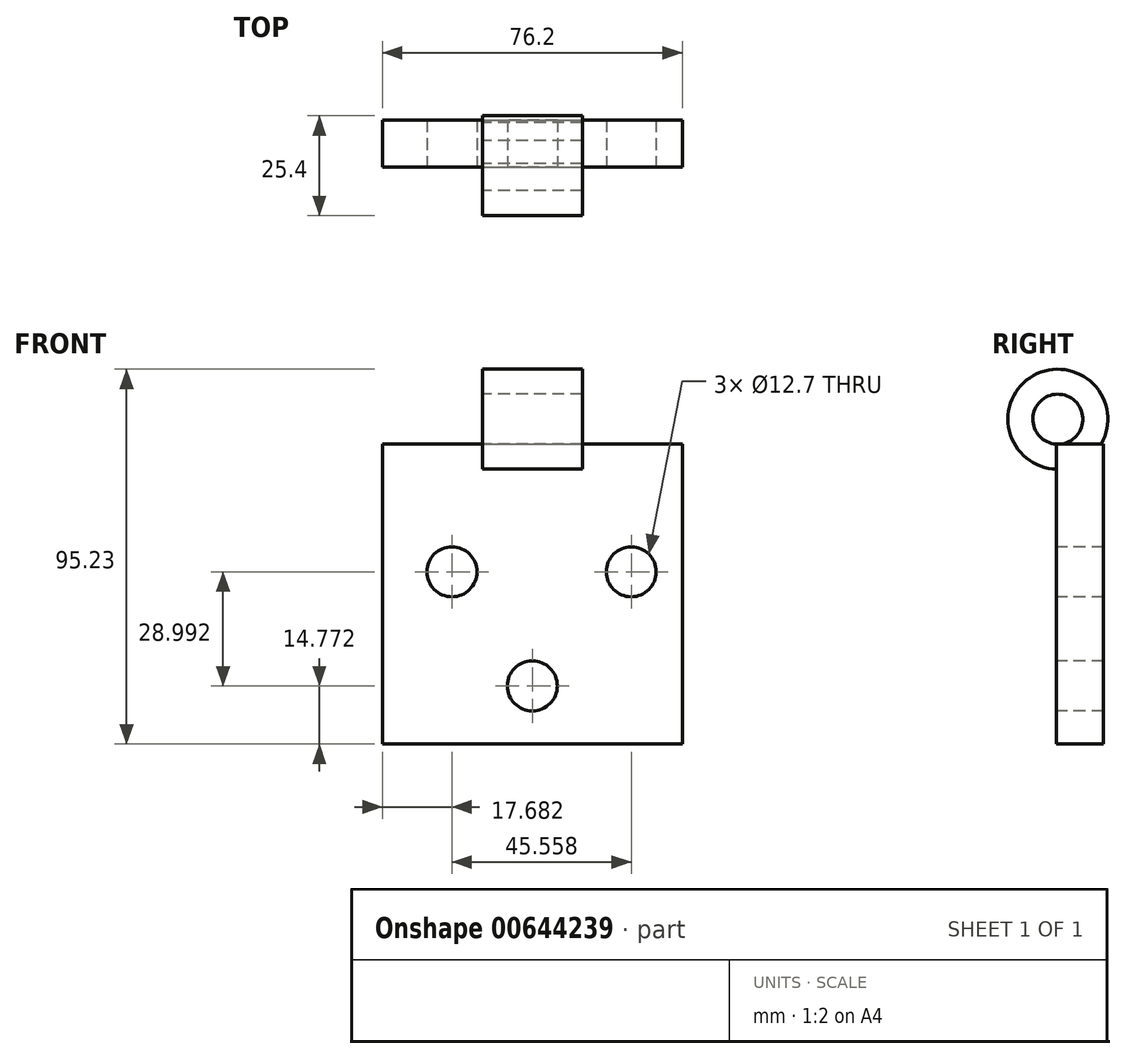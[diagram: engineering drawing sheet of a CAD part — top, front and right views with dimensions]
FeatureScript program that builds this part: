
annotation { "Feature Type Name" : "Feature", "Feature Type Description" : "" }
export const myFeature = defineFeature(function(context is Context, id is Id, definition is map)
    precondition{}
    {
        {
            var Q0;
            Q0=qCreatedBy(makeId("Front.planeOp"),FACE);
            var sketch = newSketch(context, id + "F0", { "sketchPlane" : qUnion([Q0])});
            skLineSegment(sketch, "E0.bottom", {"start": v(0, 0) * mm, "end": v(76.2, 0) * mm});
            skLineSegment(sketch, "E0.top", {"start": v(0, 76.2) * mm, "end": v(76.2, 76.2) * mm});
            skLineSegment(sketch, "E0.left", {"start": v(0, 0) * mm, "end": v(0, 76.2) * mm});
            skLineSegment(sketch, "E0.right", {"start": v(76.2, 0) * mm, "end": v(76.2, 76.2) * mm});
            skSolve(sketch);
        }
        {
            var Q0;
            Q0=qSketchRegion(id+"F0",true);
            extrude(context, id + "F1", {"entities" : qUnion([Q0]), "depth" : 11.94 * mm, "offsetDistance" : 25.4 * mm});
        }
        {
            var Q0;
            Q0=makeQuery(id+"F1.opExtrude","SWEPT_FACE",FACE,{"disambiguationData":[OSD([sQuery(id+"F0.wireOp",EDGE,"E0.left")])]});
            var sketch = newSketch(context, id + "F2", { "sketchPlane" : qUnion([Q0])});
            skCircle(sketch, "E1", {"center": v(11.6, 82.53) * mm, "radius": 12.7 * mm});
            skCircle(sketch, "E2", {"center": v(11.6, 82.53) * mm, "radius": 6.35 * mm});
            skSolve(sketch);
        }
        {
            var Q0;
            Q0=qSketchRegion(id+"F2",true);
            extrude(context, id + "F3", {"entities" : qUnion([Q0]), "operationType" : NewBodyOperationType.ADD, "oppositeDirection" : true, "depth" : 50.8 * mm, "offsetDistance" : 25.4 * mm, "hasSecondDirection" : true, "secondDirectionOppositeDirection" : true, "secondDirectionDepth" : 25.4 * mm});
        }
        {
            var Q0;
            Q0=makeQuery(id+"F1.opExtrude","CAP_FACE",FACE,{"disambiguationData":[OSD([sQuery(id+"F0.wireOp",EDGE,"E0.bottom"),sQuery(id+"F0.wireOp",EDGE,"E0.top"),sQuery(id+"F0.wireOp",EDGE,"E0.left"),sQuery(id+"F0.wireOp",EDGE,"E0.right")])],"isStart":false});
            var sketch = newSketch(context, id + "F4", { "sketchPlane" : qUnion([Q0])});
            skCircle(sketch, "E3", {"center": v(38.1, 14.77) * mm, "radius": 6.35 * mm});
            skPoint(sketch, "E3.centerSnap0", {"position": v(38.1, 69.84) * mm});
            skCircle(sketch, "E4", {"center": v(17.68, 43.76) * mm, "radius": 6.35 * mm});
            skCircle(sketch, "E5", {"center": v(63.24, 43.76) * mm, "radius": 6.35 * mm});
            skSolve(sketch);
        }
        {
            var Q0;
            Q0=qSketchRegion(id+"F4",true);
            extrude(context, id + "F5", {"entities" : qUnion([Q0]), "operationType" : NewBodyOperationType.REMOVE, "oppositeDirection" : true, "depth" : 25.4 * mm, "offsetDistance" : 25.4 * mm});
        }
    });
